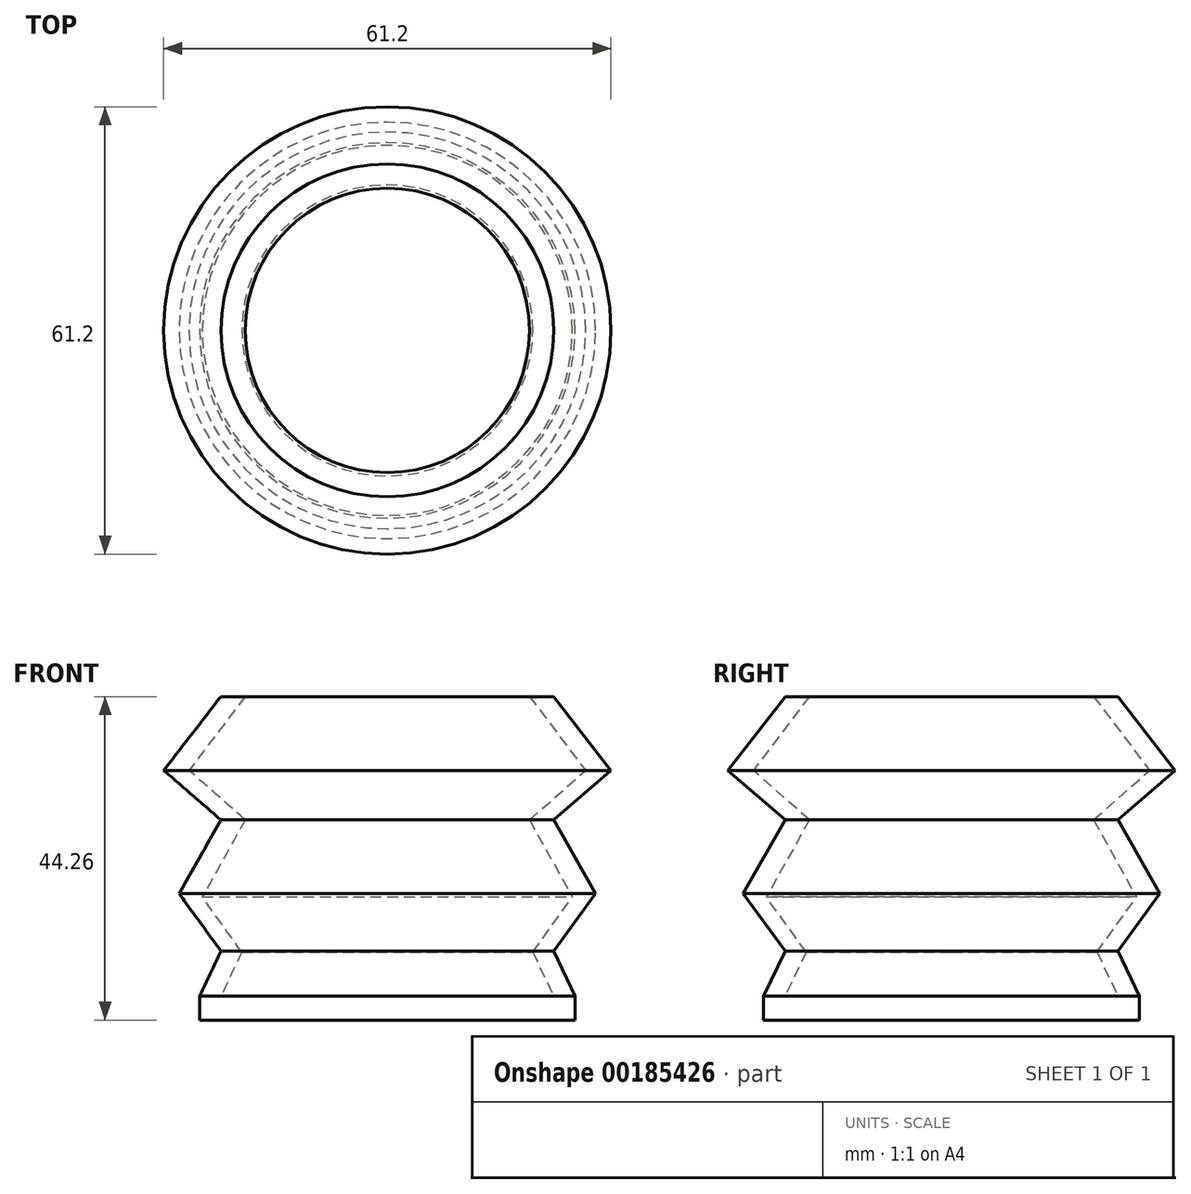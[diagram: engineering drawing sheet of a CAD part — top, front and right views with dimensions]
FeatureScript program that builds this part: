
annotation { "Feature Type Name" : "Feature", "Feature Type Description" : "" }
export const myFeature = defineFeature(function(context is Context, id is Id, definition is map)
    precondition{}
    {
        {
            var Q0;
            Q0=qCreatedBy(makeId("Front.planeOp"),FACE);
            var sketch = newSketch(context, id + "F0", { "sketchPlane" : qUnion([Q0])});
            skLineSegment(sketch, "E0", {"start": v(0, 3.28) * mm, "end": v(22.77, 3.28) * mm});
            skLineSegment(sketch, "E1", {"start": v(22.77, 3.28) * mm, "end": v(19.9, 9.3) * mm});
            skLineSegment(sketch, "E2", {"start": v(19.9, 9.3) * mm, "end": v(25.33, 16.84) * mm});
            skLineSegment(sketch, "E3", {"start": v(25.33, 16.84) * mm, "end": v(19.45, 27.39) * mm});
            skLineSegment(sketch, "E4", {"start": v(19.45, 27.39) * mm, "end": v(27.14, 34.17) * mm});
            skLineSegment(sketch, "E5", {"start": v(27.14, 34.17) * mm, "end": v(19.45, 44.26) * mm});
            skLineSegment(sketch, "E6", {"start": v(19.45, 44.26) * mm, "end": v(22.77, 44.26) * mm});
            skLineSegment(sketch, "E7", {"start": v(22.77, 44.26) * mm, "end": v(30.6, 34.17) * mm});
            skLineSegment(sketch, "E8", {"start": v(30.6, 34.17) * mm, "end": v(22.77, 27.39) * mm});
            skLineSegment(sketch, "E9", {"start": v(22.77, 27.39) * mm, "end": v(28.5, 17.3) * mm});
            skLineSegment(sketch, "E10", {"start": v(28.5, 17.3) * mm, "end": v(22.77, 9.46) * mm});
            skLineSegment(sketch, "E11", {"start": v(22.77, 9.46) * mm, "end": v(25.7, 3.28) * mm});
            skLineSegment(sketch, "E12", {"start": v(25.7, 3.28) * mm, "end": v(25.7, 0) * mm});
            skLineSegment(sketch, "E13", {"start": v(25.7, 0) * mm, "end": v(0, 0) * mm});
            skLineSegment(sketch, "E14", {"start": v(0, 0) * mm, "end": v(0, 3.28) * mm});
            skSolve(sketch);
        }
        {
            var Q0;
            Q0=makeQuery(id+"F0.imprint","IMPRINT",FACE,{"disambiguationData":[TD([[makeQuery(id+"F0.imprint","IMPRINT",EDGE,{"derivedFrom":sQuery(id+"F0.wireOp",EDGE,"E0")}),-1.0]])]});
            var Q1;
            Q1=sQuery(id+"F0.wireOp",EDGE,"E14");
            revolve(context, id + "F1", {"entities" : qUnion([Q0]), "axis" : qUnion([Q1]), "revolveType" : RevolveType.FULL});
        }
    });
